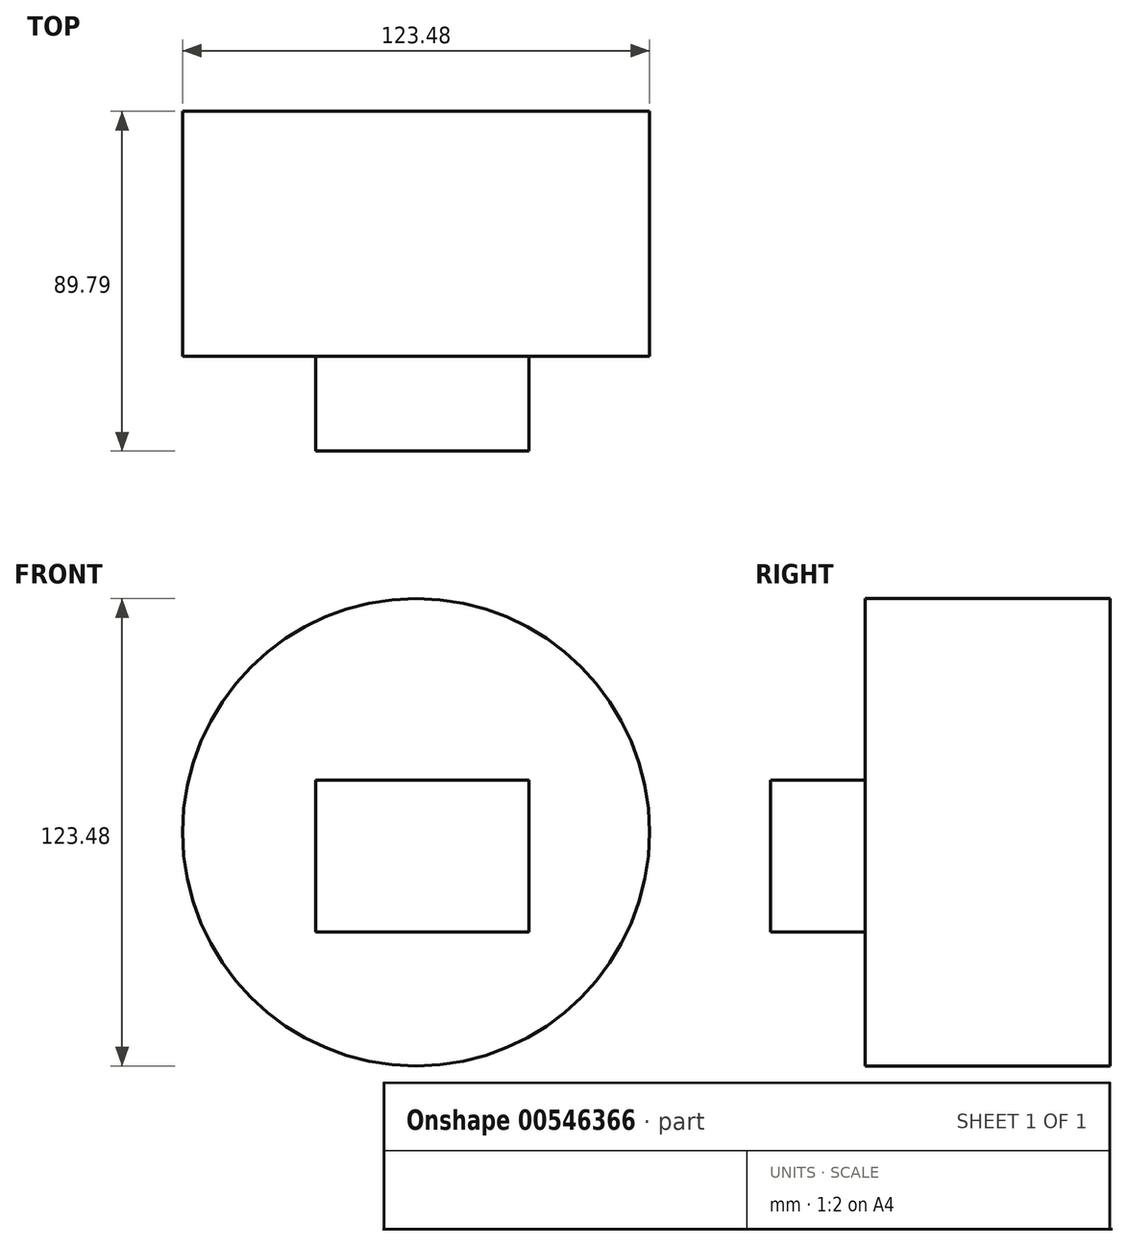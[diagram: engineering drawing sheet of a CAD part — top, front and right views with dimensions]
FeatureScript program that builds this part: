
annotation { "Feature Type Name" : "Feature", "Feature Type Description" : "" }
export const myFeature = defineFeature(function(context is Context, id is Id, definition is map)
    precondition{}
    {
        {
            var Q0;
            Q0=qCreatedBy(makeId("Front.planeOp"),FACE);
            var sketch = newSketch(context, id + "F0", { "sketchPlane" : qUnion([Q0])});
            skLineSegment(sketch, "E0.bottom", {"start": v(-26.54, 13.83) * mm, "end": v(29.9, 13.83) * mm});
            skLineSegment(sketch, "E0.top", {"start": v(-26.54, -26.4) * mm, "end": v(29.9, -26.4) * mm});
            skLineSegment(sketch, "E0.left", {"start": v(-26.54, 13.83) * mm, "end": v(-26.54, -26.4) * mm});
            skLineSegment(sketch, "E0.right", {"start": v(29.9, 13.83) * mm, "end": v(29.9, -26.4) * mm});
            skSolve(sketch);
        }
        {
            var Q0;
            Q0=makeQuery(id+"F0.imprint","IMPRINT",FACE,{"disambiguationData":[TD([[makeQuery(id+"F0.imprint","IMPRINT",EDGE,{"derivedFrom":sQuery(id+"F0.wireOp",EDGE,"E0.bottom")}),-1.0]])]});
            extrude(context, id + "F1", {"entities" : qUnion([Q0]), "depth" : 25 * mm, "offsetDistance" : 25 * mm});
        }
        {
            var Q0;
            Q0=qCreatedBy(makeId("Front.planeOp"),FACE);
            var sketch = newSketch(context, id + "F2", { "sketchPlane" : qUnion([Q0])});
            skCircle(sketch, "E1", {"center": v(0, 0) * mm, "radius": 61.74 * mm});
            skSolve(sketch);
        }
        {
            var Q0;
            Q0=makeQuery(id+"F2.imprint","IMPRINT",FACE,{"disambiguationData":[TD([[makeQuery(id+"F2.imprint","IMPRINT",EDGE,{"derivedFrom":sQuery(id+"F2.wireOp",EDGE,"E1")}),1.0]])]});
            extrude(context, id + "F3", {"entities" : qUnion([Q0]), "operationType" : NewBodyOperationType.ADD, "oppositeDirection" : true, "depth" : 64.8 * mm, "offsetDistance" : 25 * mm});
        }
    });
